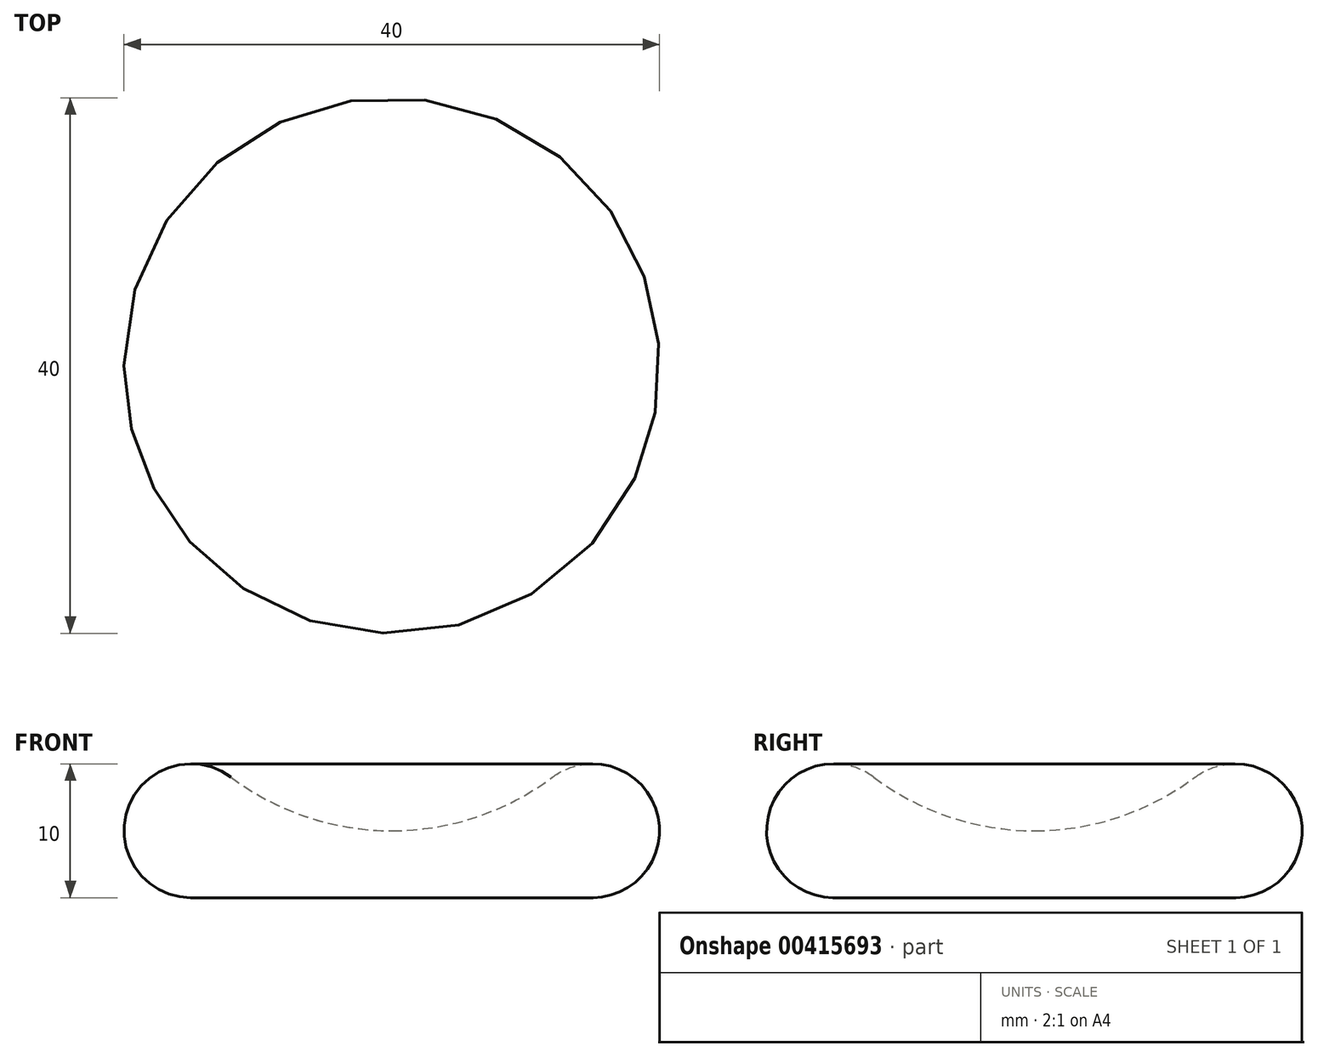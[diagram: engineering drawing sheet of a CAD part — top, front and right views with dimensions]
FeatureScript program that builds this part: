
annotation { "Feature Type Name" : "Feature", "Feature Type Description" : "" }
export const myFeature = defineFeature(function(context is Context, id is Id, definition is map)
    precondition{}
    {
        {
            var Q0;
            Q0=qCreatedBy(makeId("Front.planeOp"),FACE);
            var sketch = newSketch(context, id + "F0", { "sketchPlane" : qUnion([Q0])});
            skArc(sketch, "E0", {"start": v(-12, 5.94) * mm, "mid": v(-6.32, 2.97) * mm, "end": v(0, 1.94) * mm});
            skArc(sketch, "E1", {"start": v(-12, 5.94) * mm, "mid": v(-19.74, 3.54) * mm, "end": v(-15.04, -3.06) * mm});
            skLineSegment(sketch, "E2", {"start": v(-15.04, -3.06) * mm, "end": v(0, -3.06) * mm});
            skLineSegment(sketch, "E3", {"start": v(0, -3.06) * mm, "end": v(0, 1.94) * mm});
            skSolve(sketch);
        }
        {
            var Q0;
            Q0 = qSketchRegion(id + "F0", true);
            var Q1;
            Q1=sQuery(id+"F0.wireOp",EDGE,"E3");
            revolve(context, id + "F1", {"entities" : qUnion([Q0]), "axis" : qUnion([Q1]), "revolveType" : RevolveType.FULL});
        }
    });
